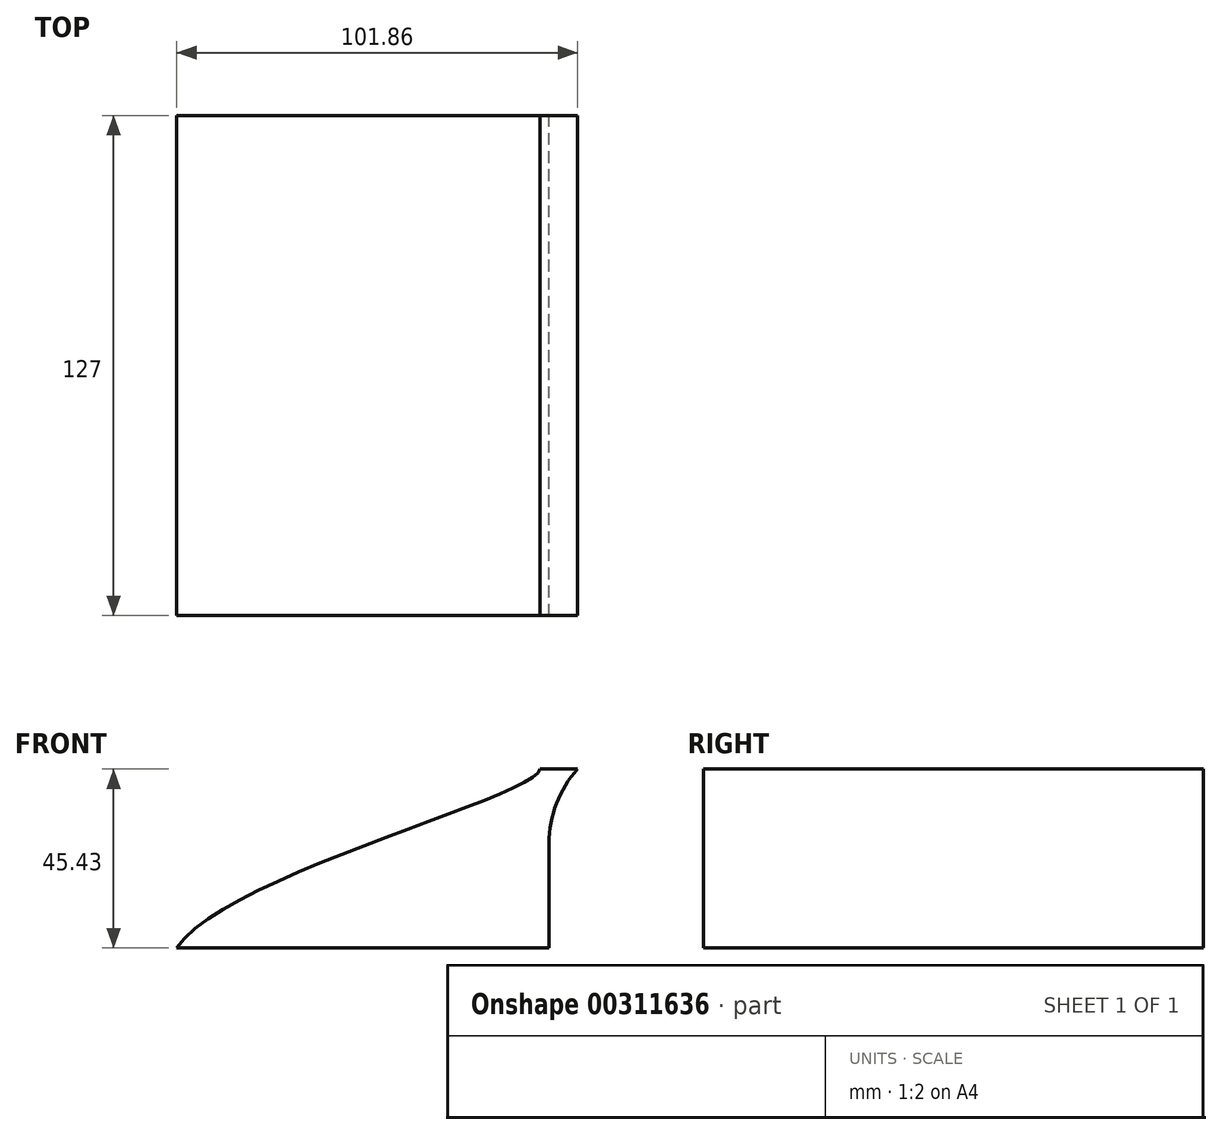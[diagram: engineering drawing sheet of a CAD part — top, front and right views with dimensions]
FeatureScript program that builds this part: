
annotation { "Feature Type Name" : "Feature", "Feature Type Description" : "" }
export const myFeature = defineFeature(function(context is Context, id is Id, definition is map)
    precondition{}
    {
        {
            var Q0;
            Q0=qCreatedBy(makeId("Front.planeOp"),FACE);
            var sketch = newSketch(context, id + "F0", { "sketchPlane" : qUnion([Q0])});
            skLineSegment(sketch, "E0.bottom", {"start": v(-23.03, 17.84) * mm, "end": v(71.57, 17.84) * mm});
            skLineSegment(sketch, "E0.top", {"start": v(-23.03, -4.15) * mm, "end": v(71.57, -4.15) * mm});
            skLineSegment(sketch, "E0.left", {"start": v(-23.03, 17.84) * mm, "end": v(-23.03, -4.15) * mm});
            skLineSegment(sketch, "E0.right", {"start": v(71.57, 17.84) * mm, "end": v(71.57, -4.15) * mm});
            skPoint(sketch, "E0.middle", {"position": v(24.27, 6.85) * mm});
            skLineSegment(sketch, "E1.bottom", {"start": v(137.34, 63.27) * mm, "end": v(86.72, 63.27) * mm});
            skLineSegment(sketch, "E1.top", {"start": v(137.34, 42.94) * mm, "end": v(86.72, 42.94) * mm});
            skLineSegment(sketch, "E1.left", {"start": v(137.34, 63.27) * mm, "end": v(137.34, 42.94) * mm});
            skLineSegment(sketch, "E1.right", {"start": v(86.72, 63.27) * mm, "end": v(86.72, 42.94) * mm});
            skPoint(sketch, "E1.middle", {"position": v(112.03, 53.1) * mm});
            skLineSegment(sketch, "E2", {"start": v(71.57, 17.84) * mm, "end": v(71.57, 44.4) * mm});
            skLineSegment(sketch, "E3", {"start": v(102.7, 63.27) * mm, "end": v(69.3, 63.27) * mm});
            skArc(sketch, "E4", {"start": v(71.57, 44.4) * mm, "mid": v(73.45, 54.5) * mm, "end": v(78.83, 63.27) * mm});
            skFitSpline(sketch, "E5", {"points": [v(-23.03, 17.84) * mm, v(69.3, 63.27) * mm, v(-34.23, 49.58) * mm, v(-46.26, 17.84) * mm, v(-44.19, 0) * mm, v(-42.32, -7.68) * mm, v(-23.03, -4.15) * mm, v(-23.03, 17.84) * mm]});
            skFitSpline(sketch, "E6", {"points": [v(-19.09, -5.6) * mm, v(71.57, -4.15) * mm], "startDerivative": vector(90.66, 1.45) * mm, "endDerivative": vector(90.66, 1.45) * mm});
            skFitSpline(sketch, "E7", {"points": [v(71.57, -4.15) * mm, v(137.34, 42.94) * mm, v(152.48, 58.5) * mm, v(137.34, 63.27) * mm], "startDerivative": vector(142.14, 100.4) * mm, "endDerivative": vector(-94.13, 13.37) * mm});
            skSolve(sketch);
        }
        {
            var Q0;
            {var subQ4=sQuery(id+"F0.wireOp",EDGE,"E0.bottom");Q0=makeQuery(id+"F0.imprint","IMPRINT",FACE,{"disambiguationData":[TD([[makeQuery(id+"F0.imprint","IMPRINT",EDGE,{"derivedFrom":subQ4}),1.0]])]});}
            extrude(context, id + "F1", {"entities" : qUnion([Q0]), "depth" : 127 * mm});
        }
    });
